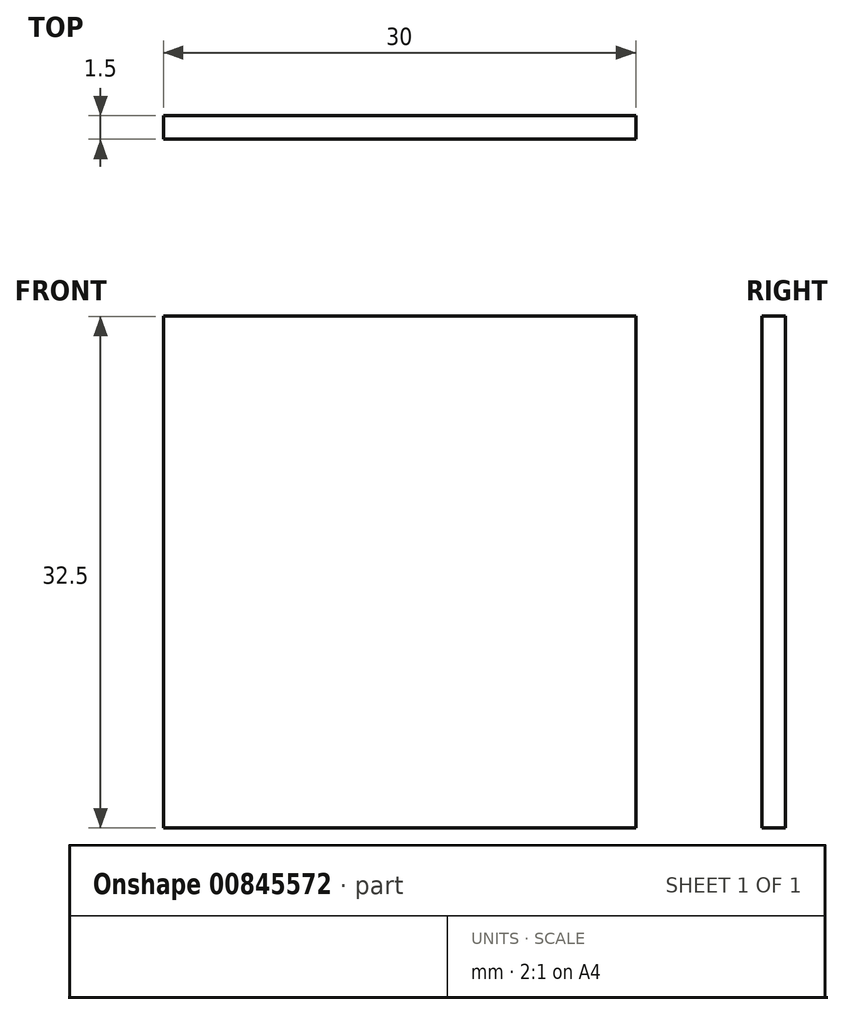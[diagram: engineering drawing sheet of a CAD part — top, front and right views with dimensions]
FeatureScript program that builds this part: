
annotation { "Feature Type Name" : "Feature", "Feature Type Description" : "" }
export const myFeature = defineFeature(function(context is Context, id is Id, definition is map)
    precondition{}
    {
        {
            var Q0;
            Q0=qCreatedBy(makeId("Front.planeOp"),FACE);
            var sketch = newSketch(context, id + "F0", { "sketchPlane" : qUnion([Q0])});
            skLineSegment(sketch, "E0.bottom", {"start": v(-20.49, 52.8) * mm, "end": v(9.51, 52.8) * mm});
            skLineSegment(sketch, "E0.top", {"start": v(-20.49, 20.3) * mm, "end": v(9.51, 20.3) * mm});
            skLineSegment(sketch, "E0.left", {"start": v(-20.49, 52.8) * mm, "end": v(-20.49, 20.3) * mm});
            skLineSegment(sketch, "E0.right", {"start": v(9.51, 52.8) * mm, "end": v(9.51, 20.3) * mm});
            skSolve(sketch);
        }
        {
            var Q0;
            Q0=makeQuery(id+"F0.imprint","IMPRINT",FACE,{"disambiguationData":[TD([[makeQuery(id+"F0.imprint","IMPRINT",EDGE,{"derivedFrom":sQuery(id+"F0.wireOp",EDGE,"E0.bottom")}),-1.0]])]});
            extrude(context, id + "F1", {"entities" : qUnion([Q0]), "depth" : 1.5 * mm, "offsetDistance" : 25 * mm});
        }
    });
